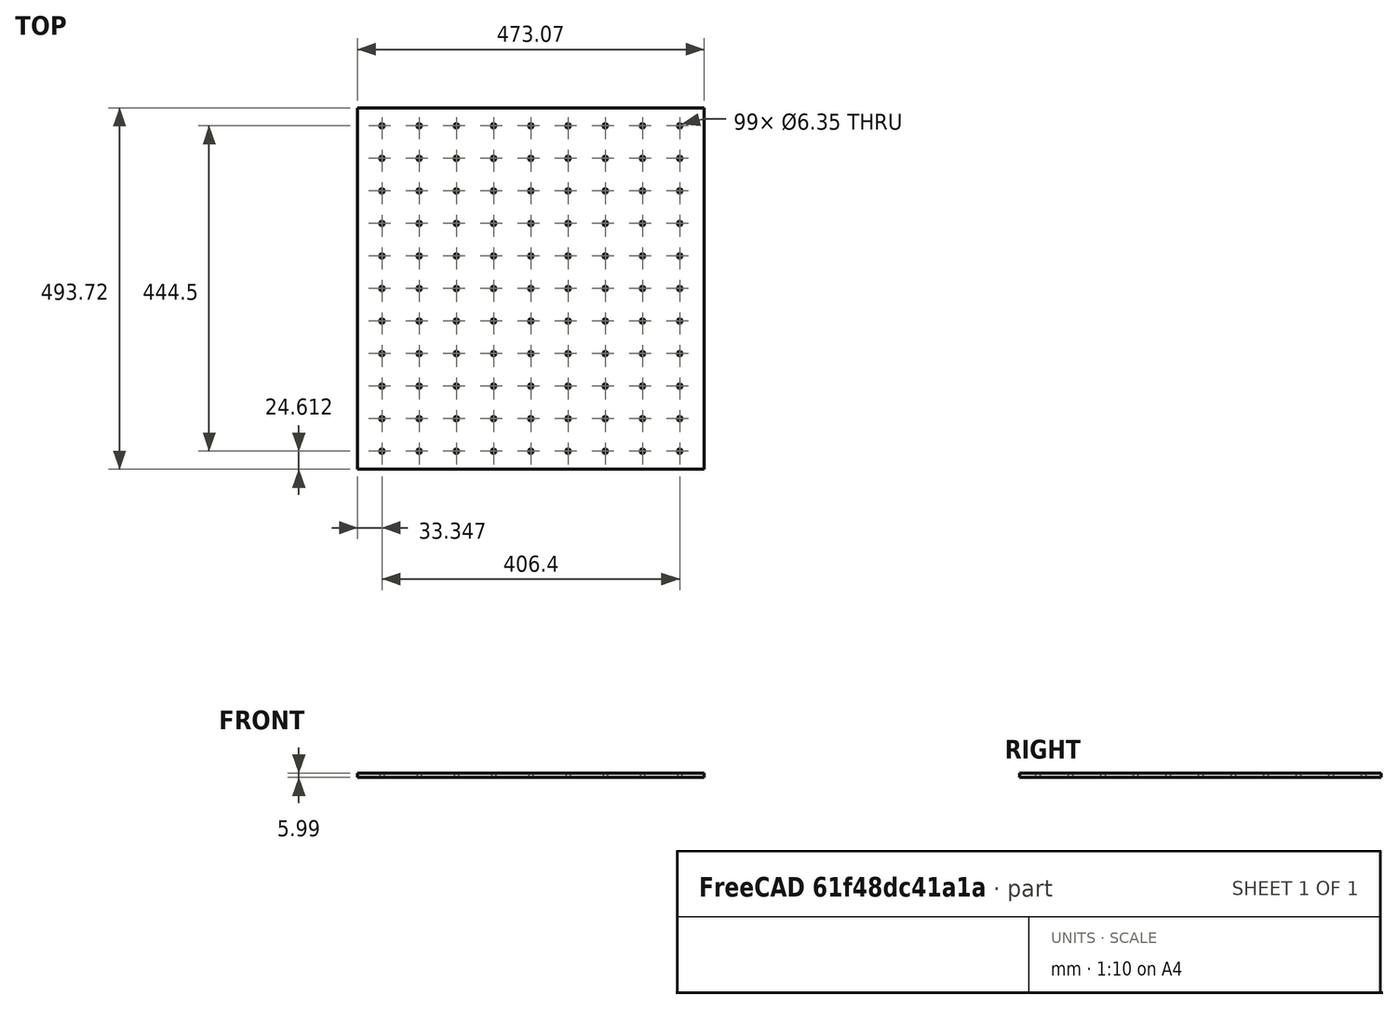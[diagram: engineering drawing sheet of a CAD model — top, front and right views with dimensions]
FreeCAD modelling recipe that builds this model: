
FCSTD DOCUMENT  (FreeCAD 0.19R24267 (Git))
Label: Up1-P1
License: All rights reserved
LicenseURL: http://en.wikipedia.org/wiki/All_rights_reserved
objects: TechDraw::DrawViewDimension×8, TechDraw::DrawViewAnnotation×6, TechDraw::DrawProjGroupItem×2, TechDraw::DrawHatch×2, Sketcher::SketchObject×1, Part::Extrusion×1, TechDraw::DrawSVGTemplate×1, TechDraw::DrawProjGroup×1, TechDraw::DrawPage×1
note: 2 computed .brp shape members not serialized (recipe doc carries the construction recipe); baked Part::Feature solids carry a one-line shape summary decoded from their .brp

FEATURE [Sketcher::SketchObject] Sketch
  FullyConstrained = false
  sketch-geometry (201):
    g0: LineSegment StartX=52.2367 StartY=147.404 StartZ=0 EndX=525.312 EndY=147.404 EndZ=0
    g1: LineSegment StartX=525.312 StartY=147.404 StartZ=0 EndX=525.312 EndY=-346.321 EndZ=0
    g2: LineSegment StartX=525.312 StartY=-346.321 StartZ=0 EndX=52.2367 EndY=-346.321 EndZ=0
    g3: LineSegment StartX=52.2367 StartY=-346.321 StartZ=0 EndX=52.2367 EndY=147.404 EndZ=0
    g4: Circle CenterX=85.5869 CenterY=122.792 CenterZ=0 NormalX=0 NormalY=0 NormalZ=1 AngleXU=0 Radius=3.175
    g5: Circle CenterX=136.387 CenterY=122.792 CenterZ=0 NormalX=0 NormalY=0 NormalZ=1 AngleXU=0 Radius=3.175
    g6: LineSegment StartX=85.5869 StartY=122.792 StartZ=0 EndX=136.387 EndY=122.792 EndZ=0
    g7: Circle CenterX=187.187 CenterY=122.792 CenterZ=0 NormalX=0 NormalY=0 NormalZ=1 AngleXU=0 Radius=3.175
    g8: LineSegment StartX=136.387 StartY=122.792 StartZ=0 EndX=187.187 EndY=122.792 EndZ=0
    g9: Circle CenterX=237.987 CenterY=122.792 CenterZ=0 NormalX=0 NormalY=0 NormalZ=1 AngleXU=0 Radius=3.175
    g10: LineSegment StartX=187.187 StartY=122.792 StartZ=0 EndX=237.987 EndY=122.792 EndZ=0
    g11: Circle CenterX=288.787 CenterY=122.792 CenterZ=0 NormalX=0 NormalY=0 NormalZ=1 AngleXU=0 Radius=3.175
    g12: LineSegment StartX=237.987 StartY=122.792 StartZ=0 EndX=288.787 EndY=122.792 EndZ=0
    g13: Circle CenterX=339.587 CenterY=122.792 CenterZ=0 NormalX=0 NormalY=0 NormalZ=1 AngleXU=0 Radius=3.175
    g14: LineSegment StartX=288.787 StartY=122.792 StartZ=0 EndX=339.587 EndY=122.792 EndZ=0
    g15: Circle CenterX=390.387 CenterY=122.792 CenterZ=0 NormalX=0 NormalY=0 NormalZ=1 AngleXU=0 Radius=3.175
    g16: LineSegment StartX=339.587 StartY=122.792 StartZ=0 EndX=390.387 EndY=122.792 EndZ=0
    g17: Circle CenterX=441.187 CenterY=122.792 CenterZ=0 NormalX=0 NormalY=0 NormalZ=1 AngleXU=0 Radius=3.175
    g18: LineSegment StartX=390.387 StartY=122.792 StartZ=0 EndX=441.187 EndY=122.792 EndZ=0
    g19: Circle CenterX=491.987 CenterY=122.792 CenterZ=0 NormalX=0 NormalY=0 NormalZ=1 AngleXU=0 Radius=3.175
    g20: LineSegment StartX=441.187 StartY=122.792 StartZ=0 EndX=491.987 EndY=122.792 EndZ=0
    g21: Circle CenterX=85.5869 CenterY=78.3418 CenterZ=0 NormalX=0 NormalY=0 NormalZ=1 AngleXU=0 Radius=3.175
    g22: LineSegment StartX=85.5869 StartY=122.792 StartZ=0 EndX=85.5869 EndY=78.3418 EndZ=0
    g23: Circle CenterX=136.387 CenterY=78.3418 CenterZ=0 NormalX=0 NormalY=0 NormalZ=1 AngleXU=0 Radius=3.175
    g24: LineSegment StartX=85.5869 StartY=78.3418 StartZ=0 EndX=136.387 EndY=78.3418 EndZ=0
    g25: Circle CenterX=187.187 CenterY=78.3418 CenterZ=0 NormalX=0 NormalY=0 NormalZ=1 AngleXU=0 Radius=3.175
    g26: LineSegment StartX=136.387 StartY=78.3418 StartZ=0 EndX=187.187 EndY=78.3418 EndZ=0
    g27: Circle CenterX=237.987 CenterY=78.3418 CenterZ=0 NormalX=0 NormalY=0 NormalZ=1 AngleXU=0 Radius=3.175
    g28: LineSegment StartX=187.187 StartY=78.3418 StartZ=0 EndX=237.987 EndY=78.3418 EndZ=0
    g29: Circle CenterX=288.787 CenterY=78.3418 CenterZ=0 NormalX=0 NormalY=0 NormalZ=1 AngleXU=0 Radius=3.175
    g30: LineSegment StartX=237.987 StartY=78.3418 StartZ=0 EndX=288.787 EndY=78.3418 EndZ=0
    g31: Circle CenterX=339.587 CenterY=78.3418 CenterZ=0 NormalX=0 NormalY=0 NormalZ=1 AngleXU=0 Radius=3.175
    g32: LineSegment StartX=288.787 StartY=78.3418 StartZ=0 EndX=339.587 EndY=78.3418 EndZ=0
    g33: Circle CenterX=390.387 CenterY=78.3418 CenterZ=0 NormalX=0 NormalY=0 NormalZ=1 AngleXU=0 Radius=3.175
    g34: LineSegment StartX=339.587 StartY=78.3418 StartZ=0 EndX=390.387 EndY=78.3418 EndZ=0
    g35: Circle CenterX=441.187 CenterY=78.3418 CenterZ=0 NormalX=0 NormalY=0 NormalZ=1 AngleXU=0 Radius=3.175
    g36: LineSegment StartX=390.387 StartY=78.3418 StartZ=0 EndX=441.187 EndY=78.3418 EndZ=0
    g37: Circle CenterX=491.987 CenterY=78.3418 CenterZ=0 NormalX=0 NormalY=0 NormalZ=1 AngleXU=0 Radius=3.175
    g38: LineSegment StartX=441.187 StartY=78.3418 StartZ=0 EndX=491.987 EndY=78.3418 EndZ=0
    g39: Circle CenterX=85.5869 CenterY=33.8918 CenterZ=0 NormalX=0 NormalY=0 NormalZ=1 AngleXU=0 Radius=3.175
    g40: LineSegment StartX=85.5869 StartY=78.3418 StartZ=0 EndX=85.5869 EndY=33.8918 EndZ=0
    g41: Circle CenterX=136.387 CenterY=33.8918 CenterZ=0 NormalX=0 NormalY=0 NormalZ=1 AngleXU=0 Radius=3.175
    g42: LineSegment StartX=85.5869 StartY=33.8918 StartZ=0 EndX=136.387 EndY=33.8918 EndZ=0
    g43: Circle CenterX=187.187 CenterY=33.8918 CenterZ=0 NormalX=0 NormalY=0 NormalZ=1 AngleXU=0 Radius=3.175
    g44: LineSegment StartX=136.387 StartY=33.8918 StartZ=0 EndX=187.187 EndY=33.8918 EndZ=0
    g45: Circle CenterX=237.987 CenterY=33.8918 CenterZ=0 NormalX=0 NormalY=0 NormalZ=1 AngleXU=0 Radius=3.175
    g46: LineSegment StartX=187.187 StartY=33.8918 StartZ=0 EndX=237.987 EndY=33.8918 EndZ=0
    g47: Circle CenterX=288.787 CenterY=33.8918 CenterZ=0 NormalX=0 NormalY=0 NormalZ=1 AngleXU=0 Radius=3.175
    g48: LineSegment StartX=237.987 StartY=33.8918 StartZ=0 EndX=288.787 EndY=33.8918 EndZ=0
    g49: Circle CenterX=339.587 CenterY=33.8918 CenterZ=0 NormalX=0 NormalY=0 NormalZ=1 AngleXU=0 Radius=3.175
    g50: LineSegment StartX=288.787 StartY=33.8918 StartZ=0 EndX=339.587 EndY=33.8918 EndZ=0
    g51: Circle CenterX=390.387 CenterY=33.8918 CenterZ=0 NormalX=0 NormalY=0 NormalZ=1 AngleXU=0 Radius=3.175
    g52: LineSegment StartX=339.587 StartY=33.8918 StartZ=0 EndX=390.387 EndY=33.8918 EndZ=0
    g53: Circle CenterX=441.187 CenterY=33.8918 CenterZ=0 NormalX=0 NormalY=0 NormalZ=1 AngleXU=0 Radius=3.175
    g54: LineSegment StartX=390.387 StartY=33.8918 StartZ=0 EndX=441.187 EndY=33.8918 EndZ=0
    g55: Circle CenterX=491.987 CenterY=33.8918 CenterZ=0 NormalX=0 NormalY=0 NormalZ=1 AngleXU=0 Radius=3.175
    g56: LineSegment StartX=441.187 StartY=33.8918 StartZ=0 EndX=491.987 EndY=33.8918 EndZ=0
    g57: Circle CenterX=85.5869 CenterY=-10.5582 CenterZ=0 NormalX=0 NormalY=0 NormalZ=1 AngleXU=0 Radius=3.175
    g58: LineSegment StartX=85.5869 StartY=33.8918 StartZ=0 EndX=85.5869 EndY=-10.5582 EndZ=0
    g59: Circle CenterX=136.387 CenterY=-10.5582 CenterZ=0 NormalX=0 NormalY=0 NormalZ=1 AngleXU=0 Radius=3.175
    g60: LineSegment StartX=85.5869 StartY=-10.5582 StartZ=0 EndX=136.387 EndY=-10.5582 EndZ=0
    g61: Circle CenterX=187.187 CenterY=-10.5582 CenterZ=0 NormalX=0 NormalY=0 NormalZ=1 AngleXU=0 Radius=3.175
    g62: LineSegment StartX=136.387 StartY=-10.5582 StartZ=0 EndX=187.187 EndY=-10.5582 EndZ=0
    g63: Circle CenterX=237.987 CenterY=-10.5582 CenterZ=0 NormalX=0 NormalY=0 NormalZ=1 AngleXU=0 Radius=3.175
    g64: LineSegment StartX=187.187 StartY=-10.5582 StartZ=0 EndX=237.987 EndY=-10.5582 EndZ=0
    g65: Circle CenterX=288.787 CenterY=-10.5582 CenterZ=0 NormalX=0 NormalY=0 NormalZ=1 AngleXU=0 Radius=3.175
    g66: LineSegment StartX=237.987 StartY=-10.5582 StartZ=0 EndX=288.787 EndY=-10.5582 EndZ=0
    g67: Circle CenterX=339.587 CenterY=-10.5582 CenterZ=0 NormalX=0 NormalY=0 NormalZ=1 AngleXU=0 Radius=3.175
    g68: LineSegment StartX=288.787 StartY=-10.5582 StartZ=0 EndX=339.587 EndY=-10.5582 EndZ=0
    g69: Circle CenterX=390.387 CenterY=-10.5582 CenterZ=0 NormalX=0 NormalY=0 NormalZ=1 AngleXU=0 Radius=3.175
    g70: LineSegment StartX=339.587 StartY=-10.5582 StartZ=0 EndX=390.387 EndY=-10.5582 EndZ=0
    g71: Circle CenterX=441.187 CenterY=-10.5582 CenterZ=0 NormalX=0 NormalY=0 NormalZ=1 AngleXU=0 Radius=3.175
    g72: LineSegment StartX=390.387 StartY=-10.5582 StartZ=0 EndX=441.187 EndY=-10.5582 EndZ=0
    g73: Circle CenterX=491.987 CenterY=-10.5582 CenterZ=0 NormalX=0 NormalY=0 NormalZ=1 AngleXU=0 Radius=3.175
    g74: LineSegment StartX=441.187 StartY=-10.5582 StartZ=0 EndX=491.987 EndY=-10.5582 EndZ=0
    g75: Circle CenterX=85.5869 CenterY=-55.0082 CenterZ=0 NormalX=0 NormalY=0 NormalZ=1 AngleXU=0 Radius=3.175
    g76: LineSegment StartX=85.5869 StartY=-10.5582 StartZ=0 EndX=85.5869 EndY=-55.0082 EndZ=0
    g77: Circle CenterX=136.387 CenterY=-55.0082 CenterZ=0 NormalX=0 NormalY=0 NormalZ=1 AngleXU=0 Radius=3.175
    g78: LineSegment StartX=85.5869 StartY=-55.0082 StartZ=0 EndX=136.387 EndY=-55.0082 EndZ=0
    g79: Circle CenterX=187.187 CenterY=-55.0082 CenterZ=0 NormalX=0 NormalY=0 NormalZ=1 AngleXU=0 Radius=3.175
    g80: LineSegment StartX=136.387 StartY=-55.0082 StartZ=0 EndX=187.187 EndY=-55.0082 EndZ=0
    g81: Circle CenterX=237.987 CenterY=-55.0082 CenterZ=0 NormalX=0 NormalY=0 NormalZ=1 AngleXU=0 Radius=3.175
    g82: LineSegment StartX=187.187 StartY=-55.0082 StartZ=0 EndX=237.987 EndY=-55.0082 EndZ=0
    g83: Circle CenterX=288.787 CenterY=-55.0082 CenterZ=0 NormalX=0 NormalY=0 NormalZ=1 AngleXU=0 Radius=3.175
    g84: LineSegment StartX=237.987 StartY=-55.0082 StartZ=0 EndX=288.787 EndY=-55.0082 EndZ=0
    g85: Circle CenterX=339.587 CenterY=-55.0082 CenterZ=0 NormalX=0 NormalY=0 NormalZ=1 AngleXU=0 Radius=3.175
    g86: LineSegment StartX=288.787 StartY=-55.0082 StartZ=0 EndX=339.587 EndY=-55.0082 EndZ=0
    g87: Circle CenterX=390.387 CenterY=-55.0082 CenterZ=0 NormalX=0 NormalY=0 NormalZ=1 AngleXU=0 Radius=3.175
    g88: LineSegment StartX=339.587 StartY=-55.0082 StartZ=0 EndX=390.387 EndY=-55.0082 EndZ=0
    g89: Circle CenterX=441.187 CenterY=-55.0082 CenterZ=0 NormalX=0 NormalY=0 NormalZ=1 AngleXU=0 Radius=3.175
    g90: LineSegment StartX=390.387 StartY=-55.0082 StartZ=0 EndX=441.187 EndY=-55.0082 EndZ=0
    g91: Circle CenterX=491.987 CenterY=-55.0082 CenterZ=0 NormalX=0 NormalY=0 NormalZ=1 AngleXU=0 Radius=3.175
    g92: LineSegment StartX=441.187 StartY=-55.0082 StartZ=0 EndX=491.987 EndY=-55.0082 EndZ=0
    g93: Circle CenterX=85.5869 CenterY=-99.4582 CenterZ=0 NormalX=0 NormalY=0 NormalZ=1 AngleXU=0 Radius=3.175
    g94: LineSegment StartX=85.5869 StartY=-55.0082 StartZ=0 EndX=85.5869 EndY=-99.4582 EndZ=0
    g95: Circle CenterX=136.387 CenterY=-99.4582 CenterZ=0 NormalX=0 NormalY=0 NormalZ=1 AngleXU=0 Radius=3.175
    g96: LineSegment StartX=85.5869 StartY=-99.4582 StartZ=0 EndX=136.387 EndY=-99.4582 EndZ=0
    g97: Circle CenterX=187.187 CenterY=-99.4582 CenterZ=0 NormalX=0 NormalY=0 NormalZ=1 AngleXU=0 Radius=3.175
    g98: LineSegment StartX=136.387 StartY=-99.4582 StartZ=0 EndX=187.187 EndY=-99.4582 EndZ=0
    g99: Circle CenterX=237.987 CenterY=-99.4582 CenterZ=0 NormalX=0 NormalY=0 NormalZ=1 AngleXU=0 Radius=3.175
    g100: LineSegment StartX=187.187 StartY=-99.4582 StartZ=0 EndX=237.987 EndY=-99.4582 EndZ=0
    g101: Circle CenterX=288.787 CenterY=-99.4582 CenterZ=0 NormalX=0 NormalY=0 NormalZ=1 AngleXU=0 Radius=3.175
    g102: LineSegment StartX=237.987 StartY=-99.4582 StartZ=0 EndX=288.787 EndY=-99.4582 EndZ=0
    g103: Circle CenterX=339.587 CenterY=-99.4582 CenterZ=0 NormalX=0 NormalY=0 NormalZ=1 AngleXU=0 Radius=3.175
    g104: LineSegment StartX=288.787 StartY=-99.4582 StartZ=0 EndX=339.587 EndY=-99.4582 EndZ=0
    g105: Circle CenterX=390.387 CenterY=-99.4582 CenterZ=0 NormalX=0 NormalY=0 NormalZ=1 AngleXU=0 Radius=3.175
    g106: LineSegment StartX=339.587 StartY=-99.4582 StartZ=0 EndX=390.387 EndY=-99.4582 EndZ=0
    g107: Circle CenterX=441.187 CenterY=-99.4582 CenterZ=0 NormalX=0 NormalY=0 NormalZ=1 AngleXU=0 Radius=3.175
    g108: LineSegment StartX=390.387 StartY=-99.4582 StartZ=0 EndX=441.187 EndY=-99.4582 EndZ=0
    g109: Circle CenterX=491.987 CenterY=-99.4582 CenterZ=0 NormalX=0 NormalY=0 NormalZ=1 AngleXU=0 Radius=3.175
    g110: LineSegment StartX=441.187 StartY=-99.4582 StartZ=0 EndX=491.987 EndY=-99.4582 EndZ=0
    g111: Circle CenterX=85.5869 CenterY=-143.908 CenterZ=0 NormalX=0 NormalY=0 NormalZ=1 AngleXU=0 Radius=3.175
    g112: LineSegment StartX=85.5869 StartY=-99.4582 StartZ=0 EndX=85.5869 EndY=-143.908 EndZ=0
    g113: Circle CenterX=136.387 CenterY=-143.908 CenterZ=0 NormalX=0 NormalY=0 NormalZ=1 AngleXU=0 Radius=3.175
    g114: LineSegment StartX=85.5869 StartY=-143.908 StartZ=0 EndX=136.387 EndY=-143.908 EndZ=0
    g115: Circle CenterX=187.187 CenterY=-143.908 CenterZ=0 NormalX=0 NormalY=0 NormalZ=1 AngleXU=0 Radius=3.175
    g116: LineSegment StartX=136.387 StartY=-143.908 StartZ=0 EndX=187.187 EndY=-143.908 EndZ=0
    g117: Circle CenterX=237.987 CenterY=-143.908 CenterZ=0 NormalX=0 NormalY=0 NormalZ=1 AngleXU=0 Radius=3.175
    g118: LineSegment StartX=187.187 StartY=-143.908 StartZ=0 EndX=237.987 EndY=-143.908 EndZ=0
    g119: Circle CenterX=288.787 CenterY=-143.908 CenterZ=0 NormalX=0 NormalY=0 NormalZ=1 AngleXU=0 Radius=3.175
    g120: LineSegment StartX=237.987 StartY=-143.908 StartZ=0 EndX=288.787 EndY=-143.908 EndZ=0
    g121: Circle CenterX=339.587 CenterY=-143.908 CenterZ=0 NormalX=0 NormalY=0 NormalZ=1 AngleXU=0 Radius=3.175
    g122: LineSegment StartX=288.787 StartY=-143.908 StartZ=0 EndX=339.587 EndY=-143.908 EndZ=0
    g123: Circle CenterX=390.387 CenterY=-143.908 CenterZ=0 NormalX=0 NormalY=0 NormalZ=1 AngleXU=0 Radius=3.175
    g124: LineSegment StartX=339.587 StartY=-143.908 StartZ=0 EndX=390.387 EndY=-143.908 EndZ=0
    g125: Circle CenterX=441.187 CenterY=-143.908 CenterZ=0 NormalX=0 NormalY=0 NormalZ=1 AngleXU=0 Radius=3.175
    g126: LineSegment StartX=390.387 StartY=-143.908 StartZ=0 EndX=441.187 EndY=-143.908 EndZ=0
    g127: Circle CenterX=491.987 CenterY=-143.908 CenterZ=0 NormalX=0 NormalY=0 NormalZ=1 AngleXU=0 Radius=3.175
    g128: LineSegment StartX=441.187 StartY=-143.908 StartZ=0 EndX=491.987 EndY=-143.908 EndZ=0
    g129: Circle CenterX=85.5869 CenterY=-188.358 CenterZ=0 NormalX=0 NormalY=0 NormalZ=1 AngleXU=0 Radius=3.175
    g130: LineSegment StartX=85.5869 StartY=-143.908 StartZ=0 EndX=85.5869 EndY=-188.358 EndZ=0
    g131: Circle CenterX=136.387 CenterY=-188.358 CenterZ=0 NormalX=0 NormalY=0 NormalZ=1 AngleXU=0 Radius=3.175
    g132: LineSegment StartX=85.5869 StartY=-188.358 StartZ=0 EndX=136.387 EndY=-188.358 EndZ=0
    g133: Circle CenterX=187.187 CenterY=-188.358 CenterZ=0 NormalX=0 NormalY=0 NormalZ=1 AngleXU=0 Radius=3.175
    g134: LineSegment StartX=136.387 StartY=-188.358 StartZ=0 EndX=187.187 EndY=-188.358 EndZ=0
    g135: Circle CenterX=237.987 CenterY=-188.358 CenterZ=0 NormalX=0 NormalY=0 NormalZ=1 AngleXU=0 Radius=3.175
    g136: LineSegment StartX=187.187 StartY=-188.358 StartZ=0 EndX=237.987 EndY=-188.358 EndZ=0
    g137: Circle CenterX=288.787 CenterY=-188.358 CenterZ=0 NormalX=0 NormalY=0 NormalZ=1 AngleXU=0 Radius=3.175
    g138: LineSegment StartX=237.987 StartY=-188.358 StartZ=0 EndX=288.787 EndY=-188.358 EndZ=0
    g139: Circle CenterX=339.587 CenterY=-188.358 CenterZ=0 NormalX=0 NormalY=0 NormalZ=1 AngleXU=0 Radius=3.175
    g140: LineSegment StartX=288.787 StartY=-188.358 StartZ=0 EndX=339.587 EndY=-188.358 EndZ=0
    g141: Circle CenterX=390.387 CenterY=-188.358 CenterZ=0 NormalX=0 NormalY=0 NormalZ=1 AngleXU=0 Radius=3.175
    g142: LineSegment StartX=339.587 StartY=-188.358 StartZ=0 EndX=390.387 EndY=-188.358 EndZ=0
    g143: Circle CenterX=441.187 CenterY=-188.358 CenterZ=0 NormalX=0 NormalY=0 NormalZ=1 AngleXU=0 Radius=3.175
    g144: LineSegment StartX=390.387 StartY=-188.358 StartZ=0 EndX=441.187 EndY=-188.358 EndZ=0
    g145: Circle CenterX=491.987 CenterY=-188.358 CenterZ=0 NormalX=0 NormalY=0 NormalZ=1 AngleXU=0 Radius=3.175
    g146: LineSegment StartX=441.187 StartY=-188.358 StartZ=0 EndX=491.987 EndY=-188.358 EndZ=0
    g147: Circle CenterX=85.5869 CenterY=-232.808 CenterZ=0 NormalX=0 NormalY=0 NormalZ=1 AngleXU=0 Radius=3.175
    g148: LineSegment StartX=85.5869 StartY=-188.358 StartZ=0 EndX=85.5869 EndY=-232.808 EndZ=0
    g149: Circle CenterX=136.387 CenterY=-232.808 CenterZ=0 NormalX=0 NormalY=0 NormalZ=1 AngleXU=0 Radius=3.175
    g150: LineSegment StartX=85.5869 StartY=-232.808 StartZ=0 EndX=136.387 EndY=-232.808 EndZ=0
    g151: Circle CenterX=187.187 CenterY=-232.808 CenterZ=0 NormalX=0 NormalY=0 NormalZ=1 AngleXU=0 Radius=3.175
    g152: LineSegment StartX=136.387 StartY=-232.808 StartZ=0 EndX=187.187 EndY=-232.808 EndZ=0
    g153: Circle CenterX=237.987 CenterY=-232.808 CenterZ=0 NormalX=0 NormalY=0 NormalZ=1 AngleXU=0 Radius=3.175
    g154: LineSegment StartX=187.187 StartY=-232.808 StartZ=0 EndX=237.987 EndY=-232.808 EndZ=0
    g155: Circle CenterX=288.787 CenterY=-232.808 CenterZ=0 NormalX=0 NormalY=0 NormalZ=1 AngleXU=0 Radius=3.175
    g156: LineSegment StartX=237.987 StartY=-232.808 StartZ=0 EndX=288.787 EndY=-232.808 EndZ=0
    g157: Circle CenterX=339.587 CenterY=-232.808 CenterZ=0 NormalX=0 NormalY=0 NormalZ=1 AngleXU=0 Radius=3.175
    g158: LineSegment StartX=288.787 StartY=-232.808 StartZ=0 EndX=339.587 EndY=-232.808 EndZ=0
    g159: Circle CenterX=390.387 CenterY=-232.808 CenterZ=0 NormalX=0 NormalY=0 NormalZ=1 AngleXU=0 Radius=3.175
    g160: LineSegment StartX=339.587 StartY=-232.808 StartZ=0 EndX=390.387 EndY=-232.808 EndZ=0
    g161: Circle CenterX=441.187 CenterY=-232.808 CenterZ=0 NormalX=0 NormalY=0 NormalZ=1 AngleXU=0 Radius=3.175
    g162: LineSegment StartX=390.387 StartY=-232.808 StartZ=0 EndX=441.187 EndY=-232.808 EndZ=0
    g163: Circle CenterX=491.987 CenterY=-232.808 CenterZ=0 NormalX=0 NormalY=0 NormalZ=1 AngleXU=0 Radius=3.175
    g164: LineSegment StartX=441.187 StartY=-232.808 StartZ=0 EndX=491.987 EndY=-232.808 EndZ=0
    g165: Circle CenterX=85.5869 CenterY=-277.258 CenterZ=0 NormalX=0 NormalY=0 NormalZ=1 AngleXU=0 Radius=3.175
    g166: LineSegment StartX=85.5869 StartY=-232.808 StartZ=0 EndX=85.5869 EndY=-277.258 EndZ=0
    g167: Circle CenterX=136.387 CenterY=-277.258 CenterZ=0 NormalX=0 NormalY=0 NormalZ=1 AngleXU=0 Radius=3.175
    g168: LineSegment StartX=85.5869 StartY=-277.258 StartZ=0 EndX=136.387 EndY=-277.258 EndZ=0
    g169: Circle CenterX=187.187 CenterY=-277.258 CenterZ=0 NormalX=0 NormalY=0 NormalZ=1 AngleXU=0 Radius=3.175
    g170: LineSegment StartX=136.387 StartY=-277.258 StartZ=0 EndX=187.187 EndY=-277.258 EndZ=0
    g171: Circle CenterX=237.987 CenterY=-277.258 CenterZ=0 NormalX=0 NormalY=0 NormalZ=1 AngleXU=0 Radius=3.175
    g172: LineSegment StartX=187.187 StartY=-277.258 StartZ=0 EndX=237.987 EndY=-277.258 EndZ=0
    g173: Circle CenterX=288.787 CenterY=-277.258 CenterZ=0 NormalX=0 NormalY=0 NormalZ=1 AngleXU=0 Radius=3.175
    g174: LineSegment StartX=237.987 StartY=-277.258 StartZ=0 EndX=288.787 EndY=-277.258 EndZ=0
    g175: Circle CenterX=339.587 CenterY=-277.258 CenterZ=0 NormalX=0 NormalY=0 NormalZ=1 AngleXU=0 Radius=3.175
    g176: LineSegment StartX=288.787 StartY=-277.258 StartZ=0 EndX=339.587 EndY=-277.258 EndZ=0
    g177: Circle CenterX=390.387 CenterY=-277.258 CenterZ=0 NormalX=0 NormalY=0 NormalZ=1 AngleXU=0 Radius=3.175
    g178: LineSegment StartX=339.587 StartY=-277.258 StartZ=0 EndX=390.387 EndY=-277.258 EndZ=0
    g179: Circle CenterX=441.187 CenterY=-277.258 CenterZ=0 NormalX=0 NormalY=0 NormalZ=1 AngleXU=0 Radius=3.175
    g180: LineSegment StartX=390.387 StartY=-277.258 StartZ=0 EndX=441.187 EndY=-277.258 EndZ=0
    g181: Circle CenterX=491.987 CenterY=-277.258 CenterZ=0 NormalX=0 NormalY=0 NormalZ=1 AngleXU=0 Radius=3.175
    g182: LineSegment StartX=441.187 StartY=-277.258 StartZ=0 EndX=491.987 EndY=-277.258 EndZ=0
    g183: Circle CenterX=85.5869 CenterY=-321.708 CenterZ=0 NormalX=0 NormalY=0 NormalZ=1 AngleXU=0 Radius=3.175
    g184: LineSegment StartX=85.5869 StartY=-277.258 StartZ=0 EndX=85.5869 EndY=-321.708 EndZ=0
    g185: Circle CenterX=136.387 CenterY=-321.708 CenterZ=0 NormalX=0 NormalY=0 NormalZ=1 AngleXU=0 Radius=3.175
    g186: LineSegment StartX=85.5869 StartY=-321.708 StartZ=0 EndX=136.387 EndY=-321.708 EndZ=0
    g187: Circle CenterX=187.187 CenterY=-321.708 CenterZ=0 NormalX=0 NormalY=0 NormalZ=1 AngleXU=0 Radius=3.175
    g188: LineSegment StartX=136.387 StartY=-321.708 StartZ=0 EndX=187.187 EndY=-321.708 EndZ=0
    g189: Circle CenterX=237.987 CenterY=-321.708 CenterZ=0 NormalX=0 NormalY=0 NormalZ=1 AngleXU=0 Radius=3.175
    g190: LineSegment StartX=187.187 StartY=-321.708 StartZ=0 EndX=237.987 EndY=-321.708 EndZ=0
    g191: Circle CenterX=288.787 CenterY=-321.708 CenterZ=0 NormalX=0 NormalY=0 NormalZ=1 AngleXU=0 Radius=3.175
    g192: LineSegment StartX=237.987 StartY=-321.708 StartZ=0 EndX=288.787 EndY=-321.708 EndZ=0
    g193: Circle CenterX=339.587 CenterY=-321.708 CenterZ=0 NormalX=0 NormalY=0 NormalZ=1 AngleXU=0 Radius=3.175
    g194: LineSegment StartX=288.787 StartY=-321.708 StartZ=0 EndX=339.587 EndY=-321.708 EndZ=0
    g195: Circle CenterX=390.387 CenterY=-321.708 CenterZ=0 NormalX=0 NormalY=0 NormalZ=1 AngleXU=0 Radius=3.175
    g196: LineSegment StartX=339.587 StartY=-321.708 StartZ=0 EndX=390.387 EndY=-321.708 EndZ=0
    g197: Circle CenterX=441.187 CenterY=-321.708 CenterZ=0 NormalX=0 NormalY=0 NormalZ=1 AngleXU=0 Radius=3.175
    g198: LineSegment StartX=390.387 StartY=-321.708 StartZ=0 EndX=441.187 EndY=-321.708 EndZ=0
    g199: Circle CenterX=491.987 CenterY=-321.708 CenterZ=0 NormalX=0 NormalY=0 NormalZ=1 AngleXU=0 Radius=3.175
    g200: LineSegment StartX=441.187 StartY=-321.708 StartZ=0 EndX=491.987 EndY=-321.708 EndZ=0
  constraints (503):
    c: Coincident(g0,g1)
    c: Coincident(g1,g2)
    c: Coincident(g2,g3)
    c: Coincident(g3,g0)
    c: Horizontal(g0)
    c: Horizontal(g2)
    c: Vertical(g1)
    c: Vertical(g3)
    c: Distance(g0,g1) = 473.075
    c: Distance(g0,g2) = 493.725
    c: Distance(g4,g0) = 24.6126
    c: Distance(g4,g3) = 33.3502
    c: Diameter(g4) = 6.35
    c: Diameter(g5) = 6.35
    c: Coincident(g4,g6)
    c: Coincident(g5,g6)
    c: Distance(g6) = 50.8
    c: Angle(g6) = 0
    c: Diameter(g7) = 6.35
    c: Coincident(g5,g8)
    c: Coincident(g7,g8)
    c: Equal(g6,g8)
    c: Parallel(g8,g6)
    c: Diameter(g9) = 6.35
    c: Coincident(g7,g10)
    c: Coincident(g9,g10)
    c: Equal(g6,g10)
    c: Parallel(g10,g6)
    c: Diameter(g11) = 6.35
    c: Coincident(g9,g12)
    c: Coincident(g11,g12)
    c: Equal(g6,g12)
    c: Parallel(g12,g6)
    c: Diameter(g13) = 6.35
    c: Coincident(g11,g14)
    c: Coincident(g13,g14)
    c: Equal(g6,g14)
    c: Parallel(g14,g6)
    c: Diameter(g15) = 6.35
    c: Coincident(g13,g16)
    c: Coincident(g15,g16)
    c: Equal(g6,g16)
    c: Parallel(g16,g6)
    c: Diameter(g17) = 6.35
    c: Coincident(g15,g18)
    c: Coincident(g17,g18)
    c: Equal(g6,g18)
    c: Parallel(g18,g6)
    c: Diameter(g19) = 6.35
    c: Coincident(g17,g20)
    c: Coincident(g19,g20)
    c: Equal(g6,g20)
    c: Parallel(g20,g6)
    c: Diameter(g21) = 6.35
    c: Coincident(g4,g22)
    c: Coincident(g21,g22)
    c: Distance(g22) = 44.45
    c: Perpendicular(g22,g6)
    c: Diameter(g23) = 6.35
    c: Coincident(g21,g24)
    c: Coincident(g23,g24)
    c: Equal(g6,g24)
    c: Parallel(g24,g6)
    c: Diameter(g25) = 6.35
    c: Coincident(g23,g26)
    c: Coincident(g25,g26)
    c: Equal(g6,g26)
    c: Parallel(g26,g6)
    c: Diameter(g27) = 6.35
    c: Coincident(g25,g28)
    c: Coincident(g27,g28)
    c: Equal(g6,g28)
    c: Parallel(g28,g6)
    c: Diameter(g29) = 6.35
    c: Coincident(g27,g30)
    c: Coincident(g29,g30)
    c: Equal(g6,g30)
    c: Parallel(g30,g6)
    c: Diameter(g31) = 6.35
    c: Coincident(g29,g32)
    c: Coincident(g31,g32)
    c: Equal(g6,g32)
    c: Parallel(g32,g6)
    c: Diameter(g33) = 6.35
    c: Coincident(g31,g34)
    c: Coincident(g33,g34)
    c: Equal(g6,g34)
    c: Parallel(g34,g6)
    c: Diameter(g35) = 6.35
    c: Coincident(g33,g36)
    c: Coincident(g35,g36)
    c: Equal(g6,g36)
    c: Parallel(g36,g6)
    c: Diameter(g37) = 6.35
    c: Coincident(g35,g38)
    c: Coincident(g37,g38)
    c: Equal(g6,g38)
    c: Parallel(g38,g6)
    c: Diameter(g39) = 6.35
    c: Coincident(g21,g40)
    c: Coincident(g39,g40)
    c: Equal(g22,g40)
    c: Perpendicular(g40,g6)
    c: Diameter(g41) = 6.35
    c: Coincident(g39,g42)
    c: Coincident(g41,g42)
    c: Equal(g6,g42)
    c: Parallel(g42,g6)
    c: Diameter(g43) = 6.35
    c: Coincident(g41,g44)
    c: Coincident(g43,g44)
    c: Equal(g6,g44)
    c: Parallel(g44,g6)
    c: Diameter(g45) = 6.35
    c: Coincident(g43,g46)
    c: Coincident(g45,g46)
    c: Equal(g6,g46)
    c: Parallel(g46,g6)
    c: Diameter(g47) = 6.35
    c: Coincident(g45,g48)
    c: Coincident(g47,g48)
    c: Equal(g6,g48)
    c: Parallel(g48,g6)
    c: Diameter(g49) = 6.35
    c: Coincident(g47,g50)
    c: Coincident(g49,g50)
    c: Equal(g6,g50)
    c: Parallel(g50,g6)
    c: Diameter(g51) = 6.35
    c: Coincident(g49,g52)
    c: Coincident(g51,g52)
    c: Equal(g6,g52)
    c: Parallel(g52,g6)
    c: Diameter(g53) = 6.35
    c: Coincident(g51,g54)
    c: Coincident(g53,g54)
    c: Equal(g6,g54)
    c: Parallel(g54,g6)
    c: Diameter(g55) = 6.35
    c: Coincident(g53,g56)
    c: Coincident(g55,g56)
    c: Equal(g6,g56)
    c: Parallel(g56,g6)
    c: Diameter(g57) = 6.35
    c: Coincident(g39,g58)
    c: Coincident(g57,g58)
    c: Equal(g22,g58)
    c: Perpendicular(g58,g6)
    c: Diameter(g59) = 6.35
    c: Coincident(g57,g60)
    c: Coincident(g59,g60)
    c: Equal(g6,g60)
    c: Parallel(g60,g6)
    c: Diameter(g61) = 6.35
    c: Coincident(g59,g62)
    c: Coincident(g61,g62)
    c: Equal(g6,g62)
    c: Parallel(g62,g6)
    c: Diameter(g63) = 6.35
    c: Coincident(g61,g64)
    c: Coincident(g63,g64)
    c: Equal(g6,g64)
    c: Parallel(g64,g6)
    c: Diameter(g65) = 6.35
    c: Coincident(g63,g66)
    c: Coincident(g65,g66)
    c: Equal(g6,g66)
    c: Parallel(g66,g6)
    c: Diameter(g67) = 6.35
    c: Coincident(g65,g68)
    c: Coincident(g67,g68)
    c: Equal(g6,g68)
    c: Parallel(g68,g6)
    c: Diameter(g69) = 6.35
    c: Coincident(g67,g70)
    c: Coincident(g69,g70)
    c: Equal(g6,g70)
    c: Parallel(g70,g6)
    c: Diameter(g71) = 6.35
    c: Coincident(g69,g72)
    c: Coincident(g71,g72)
    c: Equal(g6,g72)
    c: Parallel(g72,g6)
    c: Diameter(g73) = 6.35
    c: Coincident(g71,g74)
    c: Coincident(g73,g74)
    c: Equal(g6,g74)
    c: Parallel(g74,g6)
    c: Diameter(g75) = 6.35
    c: Coincident(g57,g76)
    c: Coincident(g75,g76)
    c: Equal(g22,g76)
    c: Perpendicular(g76,g6)
    c: Diameter(g77) = 6.35
    c: Coincident(g75,g78)
    c: Coincident(g77,g78)
    c: Equal(g6,g78)
    c: Parallel(g78,g6)
    c: Diameter(g79) = 6.35
    c: Coincident(g77,g80)
    c: Coincident(g79,g80)
    c: Equal(g6,g80)
    c: Parallel(g80,g6)
    c: Diameter(g81) = 6.35
    c: Coincident(g79,g82)
    c: Coincident(g81,g82)
    c: Equal(g6,g82)
    c: Parallel(g82,g6)
    c: Diameter(g83) = 6.35
    c: Coincident(g81,g84)
    c: Coincident(g83,g84)
    c: Equal(g6,g84)
    c: Parallel(g84,g6)
    c: Diameter(g85) = 6.35
    c: Coincident(g83,g86)
    c: Coincident(g85,g86)
    c: Equal(g6,g86)
    c: Parallel(g86,g6)
    c: Diameter(g87) = 6.35
    c: Coincident(g85,g88)
    c: Coincident(g87,g88)
    c: Equal(g6,g88)
    c: Parallel(g88,g6)
    c: Diameter(g89) = 6.35
    c: Coincident(g87,g90)
    c: Coincident(g89,g90)
    c: Equal(g6,g90)
    c: Parallel(g90,g6)
    c: Diameter(g91) = 6.35
    c: Coincident(g89,g92)
    c: Coincident(g91,g92)
    c: Equal(g6,g92)
    c: Parallel(g92,g6)
    c: Diameter(g93) = 6.35
    c: Coincident(g75,g94)
    c: Coincident(g93,g94)
    c: Equal(g22,g94)
    c: Perpendicular(g94,g6)
    c: Diameter(g95) = 6.35
    c: Coincident(g93,g96)
    c: Coincident(g95,g96)
    c: Equal(g6,g96)
    c: Parallel(g96,g6)
    c: Diameter(g97) = 6.35
    c: Coincident(g95,g98)
    c: Coincident(g97,g98)
    c: Equal(g6,g98)
    c: Parallel(g98,g6)
    c: Diameter(g99) = 6.35
    c: Coincident(g97,g100)
    c: Coincident(g99,g100)
    c: Equal(g6,g100)
    c: Parallel(g100,g6)
    c: Diameter(g101) = 6.35
    c: Coincident(g99,g102)
    c: Coincident(g101,g102)
    c: Equal(g6,g102)
    c: Parallel(g102,g6)
    c: Diameter(g103) = 6.35
    c: Coincident(g101,g104)
    c: Coincident(g103,g104)
    c: Equal(g6,g104)
    c: Parallel(g104,g6)
    c: Diameter(g105) = 6.35
    c: Coincident(g103,g106)
    c: Coincident(g105,g106)
    c: Equal(g6,g106)
    c: Parallel(g106,g6)
    c: Diameter(g107) = 6.35
    c: Coincident(g105,g108)
    c: Coincident(g107,g108)
    c: Equal(g6,g108)
    c: Parallel(g108,g6)
    c: Diameter(g109) = 6.35
    c: Coincident(g107,g110)
    c: Coincident(g109,g110)
    c: Equal(g6,g110)
    c: Parallel(g110,g6)
    c: Diameter(g111) = 6.35
    c: Coincident(g93,g112)
    c: Coincident(g111,g112)
    c: Equal(g22,g112)
    c: Perpendicular(g112,g6)
    c: Diameter(g113) = 6.35
    c: Coincident(g111,g114)
    c: Coincident(g113,g114)
    c: Equal(g6,g114)
    c: Parallel(g114,g6)
    c: Diameter(g115) = 6.35
    c: Coincident(g113,g116)
    c: Coincident(g115,g116)
    c: Equal(g6,g116)
    c: Parallel(g116,g6)
    c: Diameter(g117) = 6.35
    c: Coincident(g115,g118)
    c: Coincident(g117,g118)
    c: Equal(g6,g118)
    c: Parallel(g118,g6)
    c: Diameter(g119) = 6.35
    c: Coincident(g117,g120)
    c: Coincident(g119,g120)
    c: Equal(g6,g120)
    c: Parallel(g120,g6)
    c: Diameter(g121) = 6.35
    c: Coincident(g119,g122)
    c: Coincident(g121,g122)
    c: Equal(g6,g122)
    c: Parallel(g122,g6)
    c: Diameter(g123) = 6.35
    c: Coincident(g121,g124)
    c: Coincident(g123,g124)
    c: Equal(g6,g124)
    c: Parallel(g124,g6)
    c: Diameter(g125) = 6.35
    c: Coincident(g123,g126)
    c: Coincident(g125,g126)
    c: Equal(g6,g126)
    c: Parallel(g126,g6)
    c: Diameter(g127) = 6.35
    c: Coincident(g125,g128)
    c: Coincident(g127,g128)
    c: Equal(g6,g128)
    c: Parallel(g128,g6)
    c: Diameter(g129) = 6.35
    c: Coincident(g111,g130)
    c: Coincident(g129,g130)
    c: Equal(g22,g130)
    c: Perpendicular(g130,g6)
    c: Diameter(g131) = 6.35
    c: Coincident(g129,g132)
    c: Coincident(g131,g132)
    c: Equal(g6,g132)
    c: Parallel(g132,g6)
    c: Diameter(g133) = 6.35
    c: Coincident(g131,g134)
    c: Coincident(g133,g134)
    c: Equal(g6,g134)
    c: Parallel(g134,g6)
    c: Diameter(g135) = 6.35
    c: Coincident(g133,g136)
    c: Coincident(g135,g136)
    c: Equal(g6,g136)
    c: Parallel(g136,g6)
    c: Diameter(g137) = 6.35
    c: Coincident(g135,g138)
    c: Coincident(g137,g138)
    c: Equal(g6,g138)
    c: Parallel(g138,g6)
    c: Diameter(g139) = 6.35
    c: Coincident(g137,g140)
    c: Coincident(g139,g140)
    c: Equal(g6,g140)
    c: Parallel(g140,g6)
    c: Diameter(g141) = 6.35
    c: Coincident(g139,g142)
    c: Coincident(g141,g142)
    c: Equal(g6,g142)
    c: Parallel(g142,g6)
    c: Diameter(g143) = 6.35
    c: Coincident(g141,g144)
    c: Coincident(g143,g144)
    c: Equal(g6,g144)
    c: Parallel(g144,g6)
    c: Diameter(g145) = 6.35
    c: Coincident(g143,g146)
    c: Coincident(g145,g146)
    c: Equal(g6,g146)
    c: Parallel(g146,g6)
    c: Diameter(g147) = 6.35
    c: Coincident(g129,g148)
    c: Coincident(g147,g148)
    c: Equal(g22,g148)
    c: Perpendicular(g148,g6)
    c: Diameter(g149) = 6.35
    c: Coincident(g147,g150)
    c: Coincident(g149,g150)
    c: Equal(g6,g150)
    c: Parallel(g150,g6)
    c: Diameter(g151) = 6.35
    c: Coincident(g149,g152)
    c: Coincident(g151,g152)
    c: Equal(g6,g152)
    c: Parallel(g152,g6)
    c: Diameter(g153) = 6.35
    c: Coincident(g151,g154)
    c: Coincident(g153,g154)
    c: Equal(g6,g154)
    c: Parallel(g154,g6)
    c: Diameter(g155) = 6.35
    c: Coincident(g153,g156)
    c: Coincident(g155,g156)
    c: Equal(g6,g156)
    c: Parallel(g156,g6)
    c: Diameter(g157) = 6.35
    c: Coincident(g155,g158)
    c: Coincident(g157,g158)
    c: Equal(g6,g158)
    c: Parallel(g158,g6)
    c: Diameter(g159) = 6.35
    c: Coincident(g157,g160)
    c: Coincident(g159,g160)
    c: Equal(g6,g160)
    c: Parallel(g160,g6)
    c: Diameter(g161) = 6.35
    c: Coincident(g159,g162)
    c: Coincident(g161,g162)
    c: Equal(g6,g162)
    c: Parallel(g162,g6)
    c: Diameter(g163) = 6.35
    c: Coincident(g161,g164)
    c: Coincident(g163,g164)
    c: Equal(g6,g164)
    c: Parallel(g164,g6)
    c: Diameter(g165) = 6.35
    c: Coincident(g147,g166)
    c: Coincident(g165,g166)
    c: Equal(g22,g166)
    c: Perpendicular(g166,g6)
    c: Diameter(g167) = 6.35
    c: Coincident(g165,g168)
    c: Coincident(g167,g168)
    c: Equal(g6,g168)
    c: Parallel(g168,g6)
    c: Diameter(g169) = 6.35
    c: Coincident(g167,g170)
    c: Coincident(g169,g170)
    c: Equal(g6,g170)
    c: Parallel(g170,g6)
    c: Diameter(g171) = 6.35
    c: Coincident(g169,g172)
    c: Coincident(g171,g172)
    c: Equal(g6,g172)
    c: Parallel(g172,g6)
    c: Diameter(g173) = 6.35
    c: Coincident(g171,g174)
    c: Coincident(g173,g174)
    c: Equal(g6,g174)
    c: Parallel(g174,g6)
    c: Diameter(g175) = 6.35
    c: Coincident(g173,g176)
    c: Coincident(g175,g176)
    c: Equal(g6,g176)
    c: Parallel(g176,g6)
    c: Diameter(g177) = 6.35
    c: Coincident(g175,g178)
    c: Coincident(g177,g178)
    c: Equal(g6,g178)
    c: Parallel(g178,g6)
    c: Diameter(g179) = 6.35
    c: Coincident(g177,g180)
    c: Coincident(g179,g180)
    c: Equal(g6,g180)
    c: Parallel(g180,g6)
    c: Diameter(g181) = 6.35
    c: Coincident(g179,g182)
    c: Coincident(g181,g182)
    c: Equal(g6,g182)
    c: Parallel(g182,g6)
    c: Diameter(g183) = 6.35
    c: Coincident(g165,g184)
    c: Coincident(g183,g184)
    c: Equal(g22,g184)
    c: Perpendicular(g184,g6)
    c: Diameter(g185) = 6.35
    c: Coincident(g183,g186)
    c: Coincident(g185,g186)
    c: Equal(g6,g186)
    c: Parallel(g186,g6)
    c: Diameter(g187) = 6.35
    c: Coincident(g185,g188)
    c: Coincident(g187,g188)
    c: Equal(g6,g188)
    c: Parallel(g188,g6)
    c: Diameter(g189) = 6.35
    c: Coincident(g187,g190)
    c: Coincident(g189,g190)
    c: Equal(g6,g190)
    c: Parallel(g190,g6)
    c: Diameter(g191) = 6.35
    c: Coincident(g189,g192)
    c: Coincident(g191,g192)
    c: Equal(g6,g192)
    c: Parallel(g192,g6)
    c: Diameter(g193) = 6.35
    c: Coincident(g191,g194)
    c: Coincident(g193,g194)
    c: Equal(g6,g194)
    c: Parallel(g194,g6)
    c: Diameter(g195) = 6.35
    c: Coincident(g193,g196)
    c: Coincident(g195,g196)
    c: Equal(g6,g196)
    c: Parallel(g196,g6)
    c: Diameter(g197) = 6.35
    c: Coincident(g195,g198)
    c: Coincident(g197,g198)
    c: Equal(g6,g198)
    c: Parallel(g198,g6)
    c: Diameter(g199) = 6.35
    c: Coincident(g197,g200)
    c: Coincident(g199,g200)
    c: Equal(g6,g200)
    c: Parallel(g200,g6)
FEATURE [Part::Extrusion] Extrude
  Base = -> Sketch
  Dir = (0,0,1)
  DirMode = 2
  FaceMakerClass = Part::FaceMakerBullseye
  LengthFwd = 5.9944
  LengthRev = 0
  Solid = true
  Symmetric = false
FEATURE [TechDraw::DrawSVGTemplate] Template
  Height = 215.9
  Orientation = 1
  Width = 279.4
FEATURE [TechDraw::DrawProjGroupItem] ProjItem  label="Front"
  CoarseView = false
  Direction = (0,0,1)
  Focus = 100
  HardHidden = false
  IsoCount = 0
  IsoHidden = false
  IsoVisible = false
  LockPosition = true
  Perspective = false
  Rotation = 0
  RotationVector = (1,0,0)
  Scale = 0.25
  ScaleType = 2
  SeamHidden = false
  SeamVisible = true
  SmoothHidden = false
  SmoothVisible = true
  Source = -> [Extrude]
  Type = 0
  X = 0
  XDirection = (1,0,0)
  Y = 0
FEATURE [TechDraw::DrawProjGroupItem] ProjItem001  label="Left"
  CoarseView = false
  Direction = (-1,0,1e-16)
  Focus = 100
  HardHidden = false
  IsoCount = 0
  IsoHidden = false
  IsoVisible = false
  LockPosition = false
  Perspective = false
  Rotation = 0
  RotationVector = (1,0,0)
  ScaleType = 2
  SeamHidden = false
  SeamVisible = true
  SmoothHidden = false
  SmoothVisible = true
  Source = -> [Extrude]
  Type = 1
  X = 93.6503
  XDirection = (1e-16,0,1)
  Y = 0
FEATURE [TechDraw::DrawProjGroup] ProjGroup
  Anchor = -> ProjItem
  AutoDistribute = true
  LockPosition = false
  ProjectionType = 0
  Rotation = 0
  Scale = 0.25
  ScaleType = 2
  Source = -> [Extrude]
  Views = -> [ProjItem,ProjItem001]
  X = 126.597
  Y = 103.39
  spacingX = 15.0114
  spacingY = 15.0114
FEATURE [TechDraw::DrawViewDimension] Dimension
  Arbitrary = false
  ArbitraryTolerances = false
  EqualTolerance = true
  FormatSpec = %.3f
  FormatSpecOverTolerance = %+.3f
  FormatSpecUnderTolerance = %+.3f
  Inverted = false
  LockPosition = false
  MeasureType = 1
  OverTolerance = 0
  References2D = -> [ProjItem]
  Rotation = 0
  ScaleType = 0
  TheoreticalExact = false
  Type = 1
  UnderTolerance = 0
  X = 0.585523
  Y = -65.6704
FEATURE [TechDraw::DrawViewDimension] Dimension001
  Arbitrary = false
  ArbitraryTolerances = false
  EqualTolerance = true
  FormatSpec = %.3f
  FormatSpecOverTolerance = %+.3f
  FormatSpecUnderTolerance = %+.3f
  Inverted = false
  LockPosition = false
  MeasureType = 1
  OverTolerance = 0
  References2D = -> [ProjItem]
  Rotation = 0
  ScaleType = 0
  TheoreticalExact = false
  Type = 2
  UnderTolerance = 0
  X = 64.867
  Y = 2.88732
FEATURE [TechDraw::DrawViewDimension] Dimension002
  Arbitrary = false
  ArbitraryTolerances = false
  EqualTolerance = true
  FormatSpec = %.3f
  FormatSpecOverTolerance = %+.3f
  FormatSpecUnderTolerance = %+.3f
  Inverted = false
  LockPosition = false
  MeasureType = 1
  OverTolerance = 0
  References2D = -> [ProjItem001]
  Rotation = 0
  ScaleType = 0
  TheoreticalExact = false
  Type = 1
  UnderTolerance = 0
  X = 13.9669
  Y = 54.5462
FEATURE [TechDraw::DrawViewAnnotation] Annotation
  Font = osifont
  LineSpace = 80
  LockPosition = false
  MaxWidth = -1
  Rotation = 0
  ScaleType = 0
  Text = Repeat with equal spacing
  TextSize = 5.0038
  TextStyle = 0
  X = 122.045
  Y = 158.707
FEATURE [TechDraw::DrawViewAnnotation] Annotation001
  Font = osifont
  LineSpace = 80
  LockPosition = false
  MaxWidth = -1
  Rotation = 0
  ScaleType = 0
  Text = Repeat with equal spacing
  TextSize = 5.0038
  TextStyle = 0
  X = 122.045
  Y = 158.707
FEATURE [TechDraw::DrawViewAnnotation] Annotation003
  Font = osifont
  LineSpace = 80
  LockPosition = false
  MaxWidth = -1
  Rotation = 0
  ScaleType = 0
  Text = Figure S3 (Upright) | Panel 1 [right side interior baffle] | Quantity: 1
  TextSize = 5.0038
  TextStyle = 0
  X = 46.0561
  Y = 195.58
FEATURE [TechDraw::DrawViewAnnotation] Annotation004
  Font = osifont
  LineSpace = 80
  LockPosition = false
  MaxWidth = -1
  Rotation = 0
  ScaleType = 0
  Text = Repeat holes with same spacing and diameter
  TextSize = 5.0038
  TextStyle = 0
  X = 128.007
  Y = 178.379
FEATURE [TechDraw::DrawViewAnnotation] Annotation005
  Font = osifont
  LineSpace = 80
  LockPosition = false
  MaxWidth = -1
  Rotation = 0
  ScaleType = 0
  Text = Units: Inches
  TextSize = 5.0038
  TextStyle = 0
  X = 259.08
  Y = 5.08
FEATURE [TechDraw::DrawViewAnnotation] Annotation002
  Font = osifont
  LineSpace = 80
  LockPosition = false
  MaxWidth = -1
  Rotation = 0
  ScaleType = 0
  Text = Repeat holes with same spacing and diameter
  TextSize = 5.0038
  TextStyle = 0
  X = 141.798
  Y = 171.356
FEATURE [TechDraw::DrawViewDimension] Dimension003
  Arbitrary = false
  ArbitraryTolerances = false
  EqualTolerance = true
  FormatSpec = %.3f
  FormatSpecOverTolerance = %+.3f
  FormatSpecUnderTolerance = %+.3f
  Inverted = false
  LockPosition = false
  MeasureType = 1
  OverTolerance = 0
  References2D = -> [ProjItem]
  Rotation = 0
  ScaleType = 0
  TheoreticalExact = false
  Type = 1
  UnderTolerance = 0
  X = -74.2167
  Y = 52.5789
FEATURE [TechDraw::DrawViewDimension] Dimension004
  Arbitrary = false
  ArbitraryTolerances = false
  EqualTolerance = true
  FormatSpec = %.3f
  FormatSpecOverTolerance = %+.3f
  FormatSpecUnderTolerance = %+.3f
  Inverted = false
  LockPosition = false
  MeasureType = 1
  OverTolerance = 0
  References2D = -> [ProjItem]
  Rotation = 0
  ScaleType = 0
  TheoreticalExact = false
  Type = 2
  UnderTolerance = 0
  X = -43.444
  Y = 77.0018
FEATURE [TechDraw::DrawViewDimension] Dimension005
  Arbitrary = false
  ArbitraryTolerances = false
  EqualTolerance = true
  FormatSpec = %.3f
  FormatSpecOverTolerance = %+.3f
  FormatSpecUnderTolerance = %+.3f
  Inverted = false
  LockPosition = false
  MeasureType = 1
  OverTolerance = 0
  References2D = -> [ProjItem]
  Rotation = 0
  ScaleType = 0
  TheoreticalExact = false
  Type = 1
  UnderTolerance = 0
  X = -26.6918
  Y = 19.7612
FEATURE [TechDraw::DrawViewDimension] Dimension006
  Arbitrary = false
  ArbitraryTolerances = false
  EqualTolerance = true
  FormatSpec = %.3f
  FormatSpecOverTolerance = %+.3f
  FormatSpecUnderTolerance = %+.3f
  Inverted = false
  LockPosition = false
  MeasureType = 1
  OverTolerance = 0
  References2D = -> [ProjItem]
  Rotation = 0
  ScaleType = 0
  TheoreticalExact = false
  Type = 2
  UnderTolerance = 0
  X = -7.72741
  Y = 33.5051
FEATURE [TechDraw::DrawViewDimension] Dimension007
  Arbitrary = false
  ArbitraryTolerances = false
  EqualTolerance = true
  FormatSpec = ⌀%.3f
  FormatSpecOverTolerance = %+.3f
  FormatSpecUnderTolerance = %+.3f
  Inverted = false
  LockPosition = false
  MeasureType = 1
  OverTolerance = 0
  References2D = -> [ProjItem]
  Rotation = 0
  ScaleType = 0
  TheoreticalExact = false
  Type = 5
  UnderTolerance = 0
  X = -63.9381
  Y = 72.6821
FEATURE [TechDraw::DrawPage] Page
  KeepUpdated = true
  NextBalloonIndex = 1
  ProjectionType = 0
  Template = -> Template
  Views = -> [ProjGroup,Dimension,Dimension001,Dimension002,Annotation002,Annotation003,Annotation005,Dimension003,Dimension004,Dimension005,Dimension006,Dimension007]
FEATURE [TechDraw::DrawHatch] Hatch  label="HatchF0"
  HatchPattern = <path>
  Source = -> ProjItem [Face0]
FEATURE [TechDraw::DrawHatch] Hatch001  label="Hatch001F0"
  HatchPattern = <path>
  Source = -> ProjItem001 [Face0]
note: 2 file-system paths scrubbed to <path> (originals preserved in the JSON sidecar)
